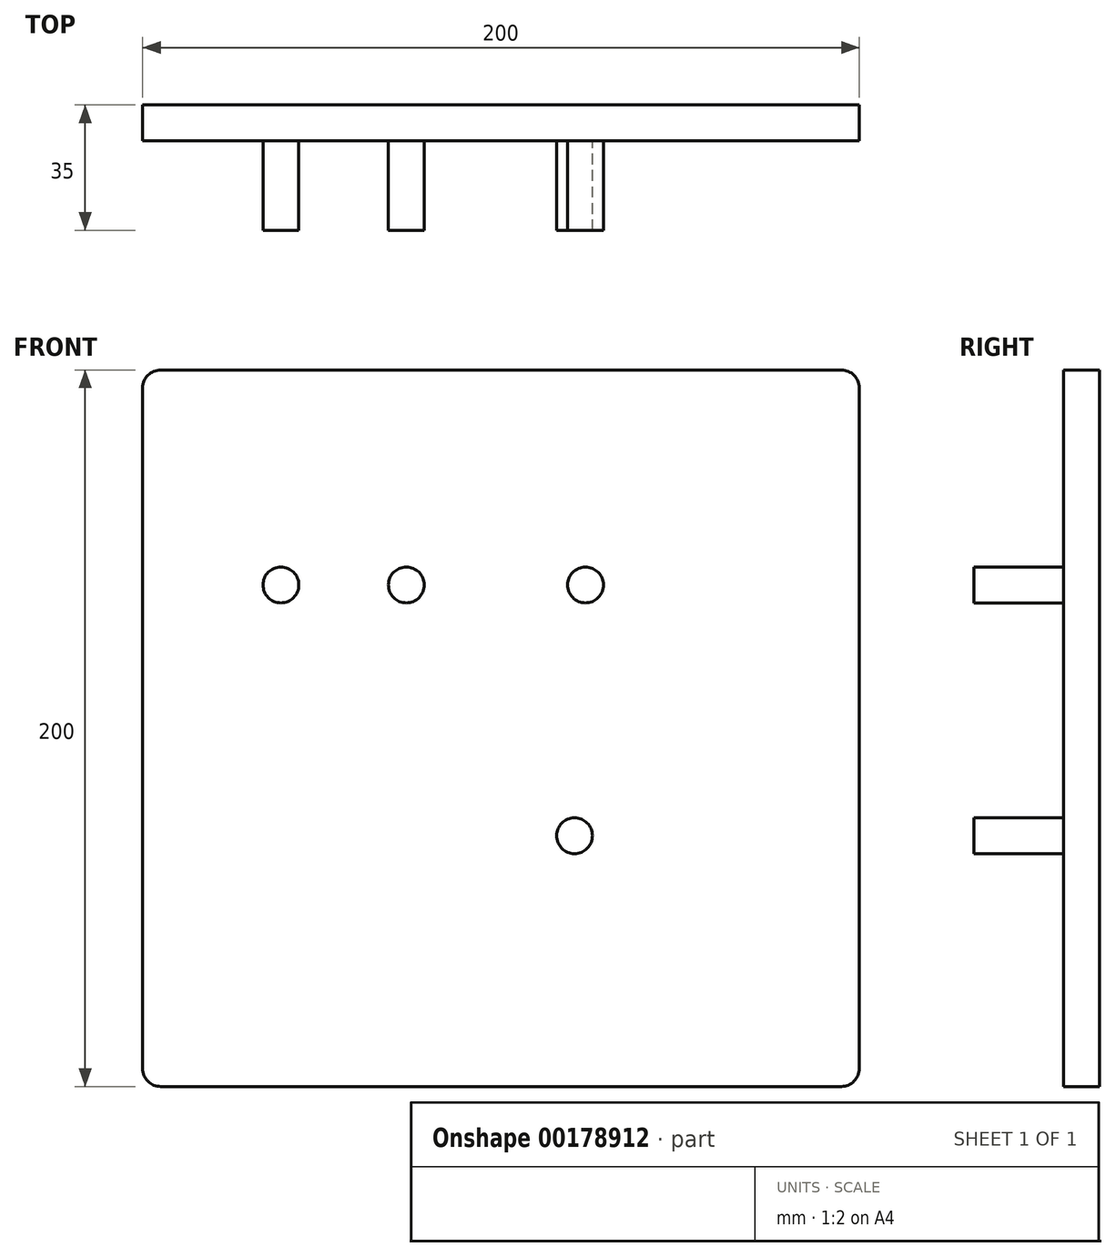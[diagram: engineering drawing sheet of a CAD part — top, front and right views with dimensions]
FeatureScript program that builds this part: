
annotation { "Feature Type Name" : "Feature", "Feature Type Description" : "" }
export const myFeature = defineFeature(function(context is Context, id is Id, definition is map)
    precondition{}
    {
        {
            var Q0;
            Q0=qCreatedBy(makeId("Front.planeOp"),FACE);
            var sketch = newSketch(context, id + "F0", { "sketchPlane" : qUnion([Q0])});
            skLineSegment(sketch, "E0.bottom", {"start": v(100, 100) * mm, "end": v(-100, 100) * mm});
            skLineSegment(sketch, "E0.top", {"start": v(100, -100) * mm, "end": v(-100, -100) * mm});
            skLineSegment(sketch, "E0.left", {"start": v(100, 100) * mm, "end": v(100, -100) * mm});
            skLineSegment(sketch, "E0.right", {"start": v(-100, 100) * mm, "end": v(-100, -100) * mm});
            skPoint(sketch, "E0.middle", {"position": v(0, 0) * mm});
            skSolve(sketch);
        }
        {
            var Q0;
            Q0=makeQuery(id+"F0.imprint","IMPRINT",FACE,{"disambiguationData":[TD([[makeQuery(id+"F0.imprint","IMPRINT",EDGE,{"derivedFrom":sQuery(id+"F0.wireOp",EDGE,"E0.bottom")}),1.0]])]});
            extrude(context, id + "F1", {"entities" : qUnion([Q0]), "depth" : 10 * mm});
        }
        {
            var Q0;
            Q0=makeQuery(id+"F1.opExtrude","SWEPT_EDGE",EDGE,{"disambiguationData":[OSD([sQuery(id+"F0.wireOp",EDGE,"E0.bottom"),sQuery(id+"F0.wireOp",EDGE,"E0.right")])]});
            var Q1;
            Q1=makeQuery(id+"F1.opExtrude","SWEPT_EDGE",EDGE,{"disambiguationData":[OSD([sQuery(id+"F0.wireOp",EDGE,"E0.top"),sQuery(id+"F0.wireOp",EDGE,"E0.right")])]});
            var Q2;
            Q2=makeQuery(id+"F1.opExtrude","SWEPT_EDGE",EDGE,{"disambiguationData":[OSD([sQuery(id+"F0.wireOp",EDGE,"E0.top"),sQuery(id+"F0.wireOp",EDGE,"E0.left")])]});
            var Q3;
            Q3=makeQuery(id+"F1.opExtrude","SWEPT_EDGE",EDGE,{"disambiguationData":[OSD([sQuery(id+"F0.wireOp",EDGE,"E0.bottom"),sQuery(id+"F0.wireOp",EDGE,"E0.left")])]});
            fillet(context, id + "F2", {"entities" : qUnion([Q0, Q1, Q2, Q3]), "radius" : 5 * mm, "tangentPropagation" : true, "allowEdgeOverflow" : false});
        }
        {
            var Q0;
            Q0=makeQuery(id+"F1.opExtrude","CAP_FACE",FACE,{"disambiguationData":[OSD([sQuery(id+"F0.wireOp",EDGE,"E0.bottom"),sQuery(id+"F0.wireOp",EDGE,"E0.top"),sQuery(id+"F0.wireOp",EDGE,"E0.left"),sQuery(id+"F0.wireOp",EDGE,"E0.right")])],"isStart":false});
            var sketch = newSketch(context, id + "F3", { "sketchPlane" : qUnion([Q0])});
            skCircle(sketch, "E1", {"center": v(-61.4, 40) * mm, "radius": 5 * mm});
            skCircle(sketch, "E2", {"center": v(-26.4, 40) * mm, "radius": 5 * mm});
            skCircle(sketch, "E3", {"center": v(23.6, 40) * mm, "radius": 5 * mm});
            skCircle(sketch, "E4", {"center": v(20.52, -30) * mm, "radius": 5 * mm});
            skSolve(sketch);
        }
        {
            var Q0;
            Q0 = qSketchRegion(id + "F3", true);
            extrude(context, id + "F4", {"entities" : qUnion([Q0]), "operationType" : NewBodyOperationType.ADD, "depth" : 25 * mm});
        }
    });
